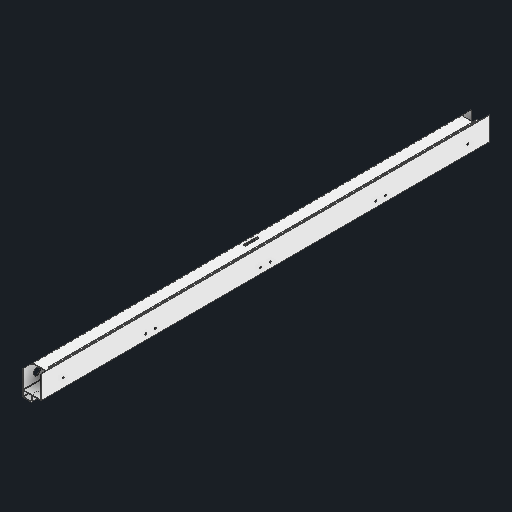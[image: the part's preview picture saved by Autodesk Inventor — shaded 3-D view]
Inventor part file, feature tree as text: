
AUTODESK INVENTOR PART (.ipt)
format: ipt  version: 2025 (Build 290162000, 162)  size: 192,000 bytes
history: native  units: in
note: dims shown in document units (in); Inventor stores cm internally (conversion verified against a paired STEP export)
features: fillet x1
ambient origin geometry x8: Origin, YZ Plane, XZ Plane, XY Plane, X Axis, Y Axis, Z Axis, Center Point
bodies: Solid1 (feature_tree)
feature tree (1):
  fillet  "Fillet13"  [1 undecoded]
note: 1 required parameter value undecoded (feature->parameter linkage not recoverable at this tier; creation-order binding heuristic only, values carry confidence <= 0.55)
